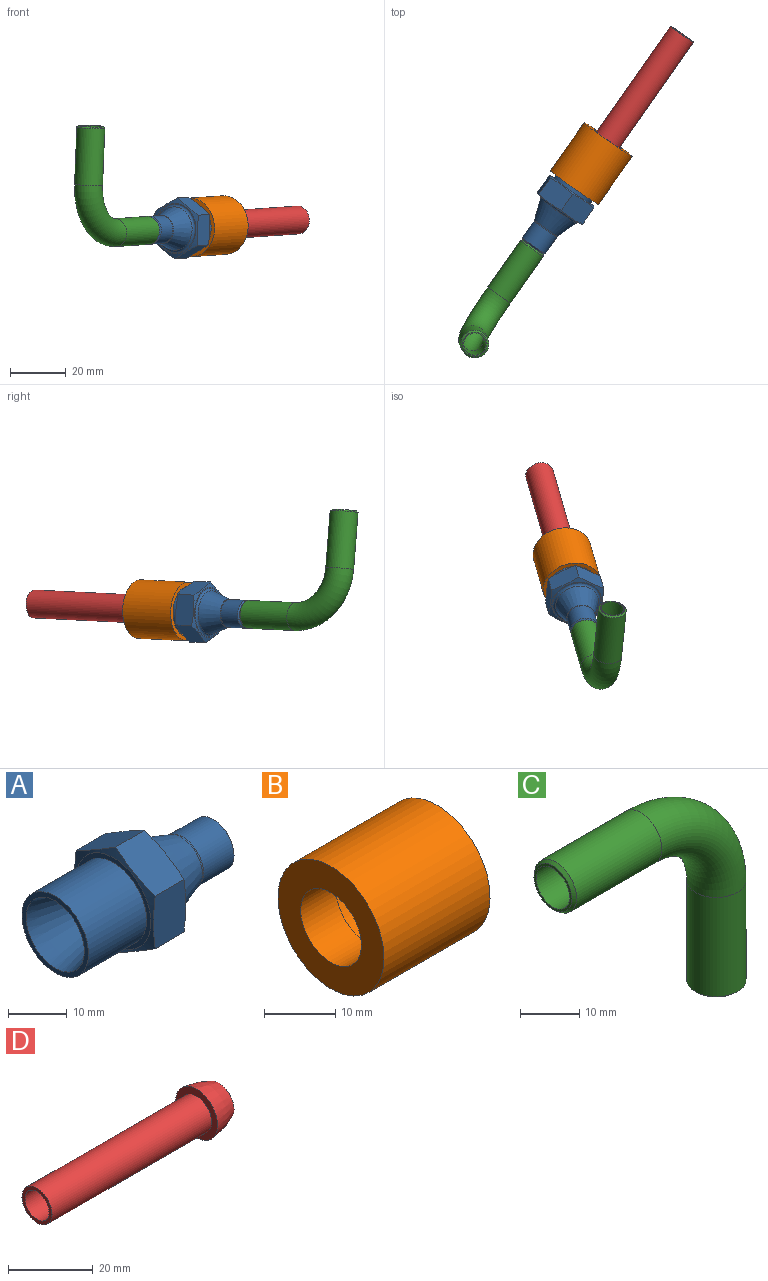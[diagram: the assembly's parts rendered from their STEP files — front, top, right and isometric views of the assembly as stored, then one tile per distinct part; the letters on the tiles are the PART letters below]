
ASSEMBLY  parts=4 mates=6
PART A: 20 faces, bbox 38.5x21.9x21.9 mm
  f0: plane 18x18mm, normal (1,0,0), area 16.3mm2, adj f11,f12
  f1: plane 18x18mm, normal (-1,0,0), area 53.4mm2, adj f6,f13
  f2: cylinder r=4mm len=27.3mm, axis (-1,0,0), area 686.2mm2, adj f3,f8
  f3: plane 8.7x8.7mm, normal (1,0,0), area 9.1mm2, adj f2,f9
  f4: cylinder r=5mm len=10mm, axis (-1,0,0), area 230.2mm2, adj f9,f10
  f5: cone r=8mm half-angle=19.4deg, axis (-1,0,0), area 327.7mm2, adj f10,f11
  f6: cylinder r=8mm len=16mm, axis (-1,0,0), area 703.7mm2, adj f1,f7
  f7: plane 16x16mm, normal (-1,0,0), area 47.1mm2, adj f6,f8
  f8: cone r=4mm half-angle=15deg, axis (-1,0,0), area 400.6mm2, adj f2,f7
  f9: cone r=5mm half-angle=52.5deg, axis (-1,0,0), area 24.1mm2, adj f3,f4
  f10: torus R=6mm, axis (-1,0,0), area 10.7mm2, adj f4,f5
  f11: torus R=8.71mm, axis (1,0,0), area 63.2mm2, adj f0,f5
  f12: cone r=9mm half-angle=75deg, axis (-1,0,0), area 60.2mm2, adj f0,f14,f15,f16,f17,f18,f19
  f13: cone r=9mm half-angle=75deg, axis (1,0,0), area 60.2mm2, adj f1,f14,f15,f16,f17,f18,f19
  f14: plane 9.5x7.73mm, normal (0,-0.5,-0.87), area 81.9mm2, adj f12,f13,f15,f19
  f15: plane 10.97x7.73mm, normal (0,-1,0), area 81.9mm2, adj f12,f13,f14,f16
  f16: plane 9.5x7.73mm, normal (0,-0.5,0.87), area 81.9mm2, adj f12,f13,f15,f17
  f17: plane 9.5x7.73mm, normal (0,0.5,0.87), area 81.9mm2, adj f12,f13,f16,f18
  f18: plane 10.97x7.73mm, normal (0,1,0), area 81.9mm2, adj f12,f13,f17,f19
  f19: plane 9.5x7.73mm, normal (0,0.5,-0.87), area 81.9mm2, adj f12,f13,f14,f18
PART B: 6 faces, bbox 21x21x21 mm
  f0: plane 21x21mm, normal (-1,0,0), area 233.3mm2, adj f1,f5
  f1: cylinder r=6mm len=12mm, axis (-1,0,0), area 263.9mm2, adj f0,f2
  f2: plane 18x18mm, normal (1,0,0), area 141.4mm2, adj f1,f3
  f3: cylinder r=9mm len=18mm, axis (-1,0,0), area 791.7mm2, adj f2,f4
  f4: plane 21x21mm, normal (1,0,0), area 91.9mm2, adj f3,f5
  f5: cylinder r=10.5mm len=21mm, axis (-1,0,0), area 1385.4mm2, adj f0,f4
PART C: 10 faces, bbox 45.9x10x45.9 mm
  f0: cylinder r=4mm len=21mm, axis (0,0,1), area 527.8mm2, adj f1,f3
  f1: torus R=18mm, axis (0,-1,0), area 710.6mm2, adj f0,f2
  f2: cylinder r=4mm len=21mm, axis (-1,0,0), area 527.8mm2, adj f1,f4
  f3: plane 8.7x8.7mm, normal (0,0,-1), area 9.1mm2, adj f0,f8
  f4: plane 9x9mm, normal (-1,0,0), area 13.4mm2, adj f2,f9
  f5: cylinder r=5mm len=20.5mm, axis (0,0,1), area 644mm2, adj f6,f8
  f6: torus R=18mm, axis (0,-1,0), area 888.3mm2, adj f5,f7
  f7: cylinder r=5mm len=20.35mm, axis (-1,0,0), area 639.3mm2, adj f6,f9
  f8: cone r=5mm half-angle=52.5deg, axis (0,0,1), area 24.1mm2, adj f3,f5
  f9: cone r=4.5mm half-angle=37.5deg, axis (1,0,0), area 24.5mm2, adj f4,f7
PART D: 6 faces, bbox 60.6x14x14 mm
  f0: plane 10x10mm, normal (-1,0,0), area 28.3mm2, adj f1,f5
  f1: cylinder r=4mm len=60.6mm, axis (-1,0,0), area 1523.2mm2, adj f0,f2
  f2: plane 10x10mm, normal (1,0,0), area 28.3mm2, adj f1,f3
  f3: revolved ~14x14mm, area 305mm2, adj f2,f4
  f4: plane 14x14mm, normal (-1,0,0), area 75.4mm2, adj f3,f5
  f5: cylinder r=5mm len=53.14mm, axis (-1,0,0), area 1669.5mm2, adj f0,f4
PLACE A rot(axis=(-0.46,0.89,0.04),180deg) t=(-194.33,11.2,-7.98)mm
PLACE B rot(axis=(-0.41,0.81,-0.42),153.3deg) t=(-167.42,49.63,-6.12)mm
PLACE C rot(axis=(-0.46,0.89,0.04),180deg) t=(-215.14,-23.69,29.32)mm
PLACE D rot(axis=(0,0.05,-1),125deg) t=(-175.71,37.79,-6.7)mm
MATE planar C.f9 <-> A.f2  axis (0.57,0.82,0.04) through (-194.33,11.2,-7.98)mm
MATE planar B.f1 <-> D.f1  axis (-0.57,-0.82,-0.04) through (-171.43,43.9,-6.4)mm
MATE cylindrical C.f9 <-> D.f1  axis (0.57,0.82,0.04) through (-200.54,2.34,-8.41)mm
MATE cylindrical B.f1 <-> D.f1  axis (0.57,0.82,0.04) through (-173.44,41.04,-6.54)mm
MATE planar A.f2 <-> D.f1  axis (0.57,0.82,0.04) through (-172.26,42.71,-6.46)mm
MATE cylindrical A.f2 <-> D.f1  axis (0.57,0.82,0.04) through (-191.94,14.61,-7.82)mm
